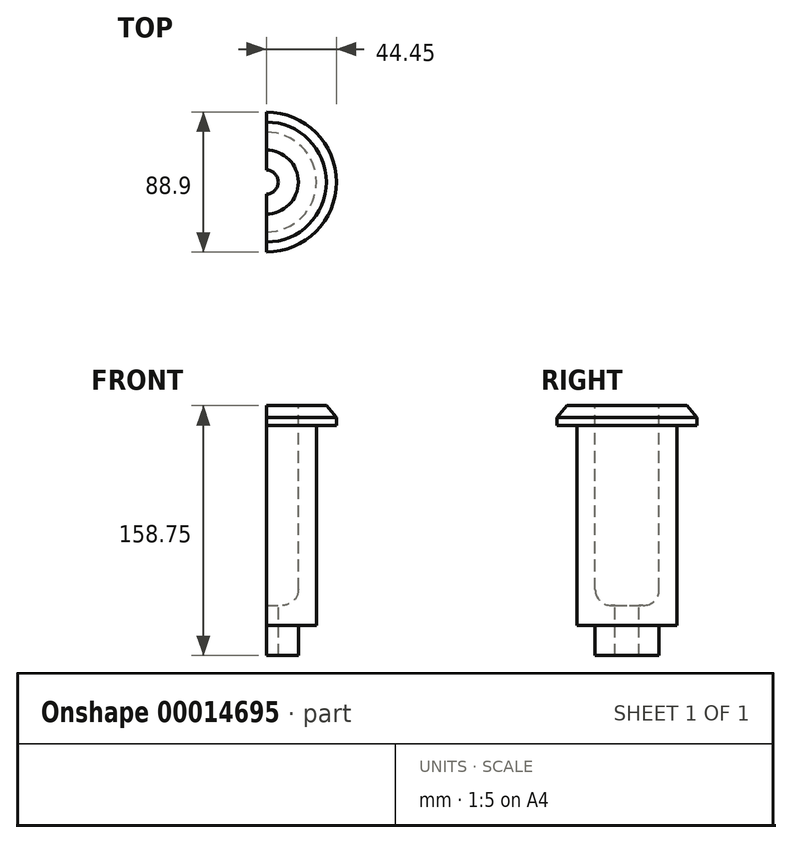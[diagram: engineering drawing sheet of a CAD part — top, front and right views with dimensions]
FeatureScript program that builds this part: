
annotation { "Feature Type Name" : "Feature", "Feature Type Description" : "" }
export const myFeature = defineFeature(function(context is Context, id is Id, definition is map)
    precondition{}
    {
        {
            var Q0;
            Q0=qCreatedBy(makeId("Front.planeOp"),FACE);
            var sketch = newSketch(context, id + "F0", { "sketchPlane" : qUnion([Q0])});
            skLineSegment(sketch, "E0", {"start": v(20.32, 110.8) * mm, "end": v(20.32, -171.83) * mm, "construction": true});
            skLineSegment(sketch, "E1", {"start": v(31.75, 109.92) * mm, "end": v(31.75, -17.26) * mm, "construction": true});
            skLineSegment(sketch, "E2", {"start": v(31.75, 63.5) * mm, "end": v(31.75, -63.5) * mm});
            skPoint(sketch, "E3", {"position": v(31.75, 0) * mm});
            skLineSegment(sketch, "E4", {"start": v(0, 63.5) * mm, "end": v(48.76, 63.5) * mm});
            skLineSegment(sketch, "E5", {"start": v(48.76, 63.5) * mm, "end": v(38.1, 76.2) * mm});
            skLineSegment(sketch, "E6", {"start": v(38.1, 76.2) * mm, "end": v(0, 76.2) * mm});
            skLineSegment(sketch, "E7", {"start": v(40.67, -63.5) * mm, "end": v(20.32, -63.5) * mm});
            skLineSegment(sketch, "E8", {"start": v(20.32, -63.5) * mm, "end": v(20.32, -82.55) * mm});
            skLineSegment(sketch, "E9", {"start": v(20.32, -82.55) * mm, "end": v(7.62, -82.55) * mm});
            skLineSegment(sketch, "E10", {"start": v(7.62, -82.55) * mm, "end": v(7.62, -50.8) * mm});
            skLineSegment(sketch, "E11", {"start": v(20.32, 76.2) * mm, "end": v(20.32, -40.64) * mm});
            skLineSegment(sketch, "E12", {"start": v(10.16, -50.8) * mm, "end": v(7.62, -50.8) * mm});
            skPoint(sketch, "E13", {"position": v(20.32, -30.52) * mm});
            skPoint(sketch, "E14.visualSharp", {"position": v(20.32, -50.8) * mm});
            skArc(sketch, "E14.filletArc", {"start": v(10.16, -50.8) * mm, "mid": v(17.34, -47.82) * mm, "end": v(20.32, -40.64) * mm});
            skLineSegment(sketch, "E15", {"start": v(0, 183.83) * mm, "end": v(0, -164.94) * mm, "construction": true});
            skLineSegment(sketch, "E16", {"start": v(126.06, 31.75) * mm, "end": v(-86.14, 31.75) * mm, "construction": true});
            skLineSegment(sketch, "E17", {"start": v(89.96, 0) * mm, "end": v(-60.79, 0) * mm, "construction": true});
            skLineSegment(sketch, "E18.MirrorCS", {"start": v(126.06, -31.75) * mm, "end": v(-86.14, -31.75) * mm, "construction": true});
            skSolve(sketch);
        }
        {
            var Q0;
            {var subQ1=sQuery(id+"F0.wireOp",EDGE,"E5");Q0=makeQuery(id+"F0.imprint","IMPRINT",FACE,{"disambiguationData":[TD([[makeQuery(id+"F0.imprint","IMPRINT",EDGE,{"derivedFrom":subQ1}),1.0]])]});}
            var Q1;
            {var subQ2=sQuery(id+"F0.wireOp",EDGE,"E2");Q1=makeQuery(id+"F0.imprint","IMPRINT",FACE,{"disambiguationData":[TD([[makeQuery(id+"F0.imprint","IMPRINT",EDGE,{"derivedFrom":subQ2}),-1.0]])]});}
            var Q2;
            Q2=sQuery(id+"F0.wireOp",EDGE,"E15");
            revolve(context, id + "F1", {"entities" : qUnion([Q0, Q1]), "axis" : qUnion([Q2]), "revolveType" : RevolveType.FULL});
        }
        {
            var Q0;
            Q0=makeQuery(id+"F1.opRevolve","SWEPT_FACE",FACE,{"disambiguationData":[OSD([sQuery(id+"F0.wireOp",EDGE,"E4")])]});
            var sketch = newSketch(context, id + "F2", { "sketchPlane" : qUnion([Q0])});
            skCircle(sketch, "E19", {"center": v(0, 0) * mm, "radius": 44.45 * mm});
            skCircle(sketch, "E20", {"center": v(0, 0) * mm, "radius": 82.41 * mm});
            skSolve(sketch);
        }
        {
            var Q0;
            Q0=makeQuery(id+"F2.imprint","IMPRINT",FACE,{"disambiguationData":[TD([[makeQuery(id+"F2.imprint","IMPRINT",EDGE,{"derivedFrom":sQuery(id+"F2.wireOp",EDGE,"E19")}),-1.0]])]});
            extrude(context, id + "F3", {"entities" : qUnion([Q0]), "operationType" : NewBodyOperationType.REMOVE, "endBound" : BoundingType.THROUGH_ALL, "oppositeDirection" : true, "depth" : 25.4 * mm});
        }
        {
            var Q0;
            Q0=qCreatedBy(makeId("Right.planeOp"),FACE);
            var sketch = newSketch(context, id + "F4", { "sketchPlane" : qUnion([Q0])});
            skLineSegment(sketch, "E21.bottom", {"start": v(-152.4, 134.26) * mm, "end": v(100.2, 134.26) * mm});
            skLineSegment(sketch, "E21.top", {"start": v(-152.4, -149.6) * mm, "end": v(100.2, -149.6) * mm});
            skLineSegment(sketch, "E21.left", {"start": v(-152.4, 134.26) * mm, "end": v(-152.4, -149.6) * mm});
            skLineSegment(sketch, "E21.right", {"start": v(100.2, 134.26) * mm, "end": v(100.2, -149.6) * mm});
            skSolve(sketch);
        }
        {
            var Q0;
            Q0=makeQuery(id+"F4.imprint","IMPRINT",FACE,{"disambiguationData":[TD([[makeQuery(id+"F4.imprint","IMPRINT",EDGE,{"derivedFrom":sQuery(id+"F4.wireOp",EDGE,"E21.bottom")}),-1.0]])]});
            extrude(context, id + "F5", {"entities" : qUnion([Q0]), "operationType" : NewBodyOperationType.REMOVE, "endBound" : BoundingType.THROUGH_ALL, "oppositeDirection" : true, "depth" : 25.4 * mm});
        }
    });
